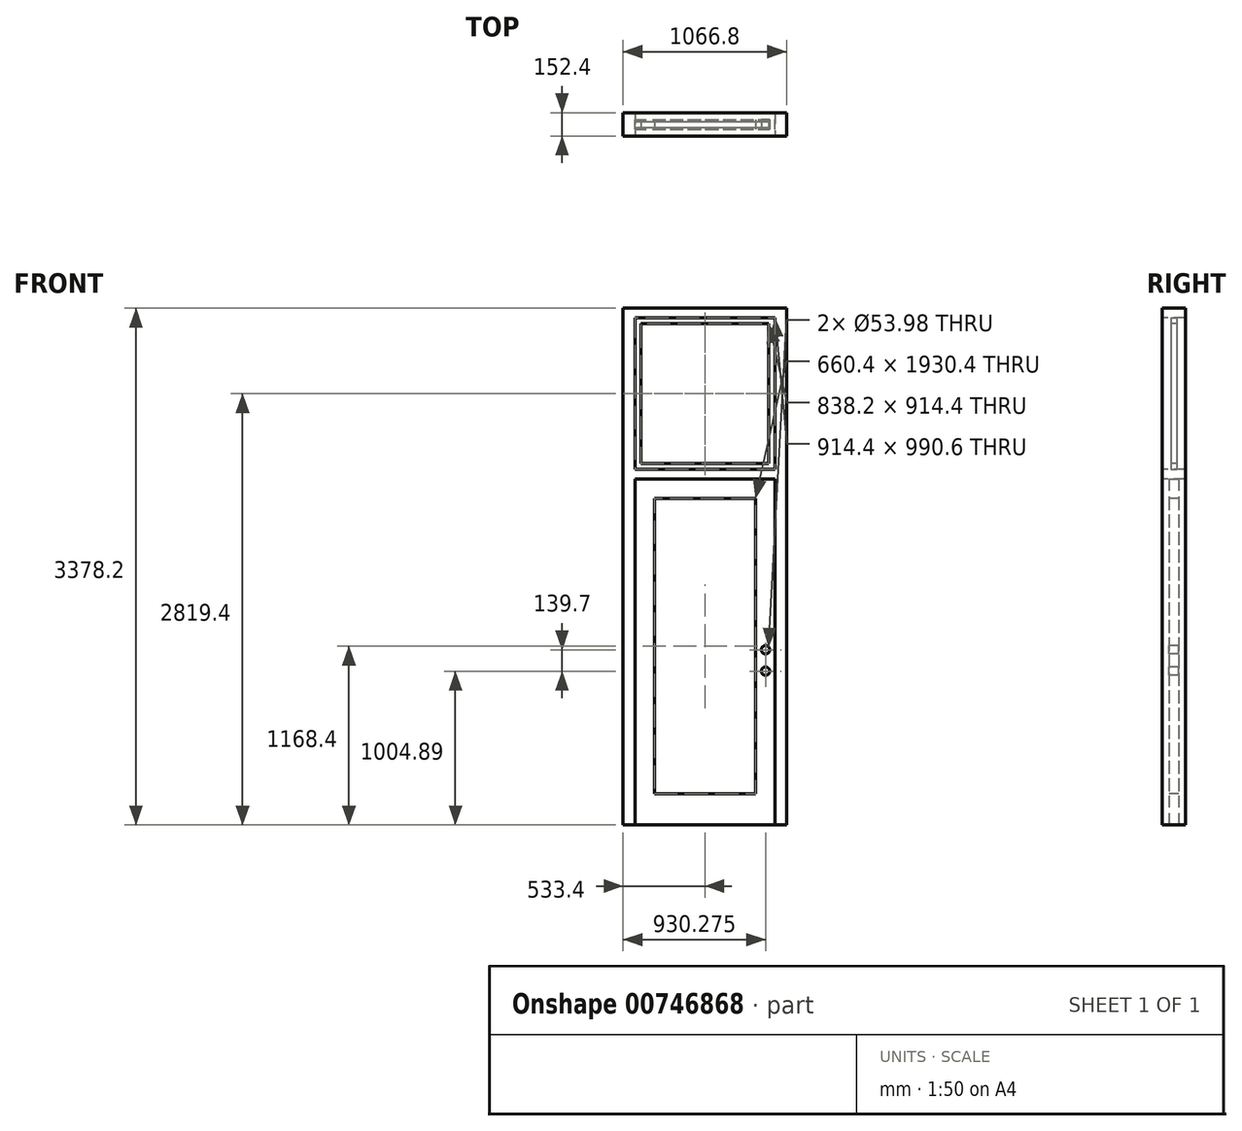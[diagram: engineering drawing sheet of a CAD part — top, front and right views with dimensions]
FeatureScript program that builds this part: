
annotation { "Feature Type Name" : "Feature", "Feature Type Description" : "" }
export const myFeature = defineFeature(function(context is Context, id is Id, definition is map)
    precondition{}
    {
        {
            var Q0;
            Q0=qCreatedBy(makeId("Front.planeOp"),FACE);
            var sketch = newSketch(context, id + "F0", { "sketchPlane" : qUnion([Q0])});
            skLineSegment(sketch, "E0.bottom", {"start": v(-533.4, 1689.1) * mm, "end": v(533.4, 1689.1) * mm});
            skLineSegment(sketch, "E0.top", {"start": v(-533.4, -1689.1) * mm, "end": v(533.4, -1689.1) * mm});
            skLineSegment(sketch, "E0.left", {"start": v(-533.4, 1689.1) * mm, "end": v(-533.4, -1689.1) * mm});
            skLineSegment(sketch, "E0.right", {"start": v(533.4, 1689.1) * mm, "end": v(533.4, -1689.1) * mm});
            skLineSegment(sketch, "E1", {"start": v(0, 1689.1) * mm, "end": v(0, 0) * mm, "construction": true});
            skLineSegment(sketch, "E2", {"start": v(0, 0) * mm, "end": v(-533.4, 0) * mm, "construction": true});
            skSolve(sketch);
        }
        {
            var Q0;
            Q0=makeQuery(id+"F0.imprint","IMPRINT",FACE,{"disambiguationData":[TD([[makeQuery(id+"F0.imprint","IMPRINT",EDGE,{"derivedFrom":sQuery(id+"F0.wireOp",EDGE,"E0.bottom")}),-1.0]])]});
            extrude(context, id + "F1", {"entities" : qUnion([Q0]), "endBound" : BoundingType.SYMMETRIC, "depth" : 152.4 * mm, "offsetDistance" : 25.4 * mm});
        }
        {
            var Q0;
            Q0=makeQuery(id+"F1.opExtrude","CAP_FACE",FACE,{"disambiguationData":[OSD([sQuery(id+"F0.wireOp",EDGE,"E0.bottom"),sQuery(id+"F0.wireOp",EDGE,"E0.top"),sQuery(id+"F0.wireOp",EDGE,"E0.left"),sQuery(id+"F0.wireOp",EDGE,"E0.right")])],"isStart":false});
            var sketch = newSketch(context, id + "F2", { "sketchPlane" : qUnion([Q0])});
            skLineSegment(sketch, "E3.bottom", {"start": v(-457.2, 571.5) * mm, "end": v(457.2, 571.5) * mm});
            skLineSegment(sketch, "E3.top", {"start": v(-457.2, -1689.1) * mm, "end": v(457.2, -1689.1) * mm});
            skLineSegment(sketch, "E3.left", {"start": v(-457.2, 571.5) * mm, "end": v(-457.2, -1689.1) * mm});
            skLineSegment(sketch, "E3.right", {"start": v(457.2, 571.5) * mm, "end": v(457.2, -1689.1) * mm});
            skLineSegment(sketch, "E4.bottom", {"start": v(-457.2, 1625.6) * mm, "end": v(457.2, 1625.6) * mm});
            skLineSegment(sketch, "E4.top", {"start": v(-457.2, 635) * mm, "end": v(457.2, 635) * mm});
            skLineSegment(sketch, "E4.left", {"start": v(-457.2, 1625.6) * mm, "end": v(-457.2, 635) * mm});
            skLineSegment(sketch, "E4.right", {"start": v(457.2, 1625.6) * mm, "end": v(457.2, 635) * mm});
            skLineSegment(sketch, "E5", {"start": v(0, 571.5) * mm, "end": v(0, 0) * mm, "construction": true});
            skSolve(sketch);
        }
        {
            var Q0;
            Q0 = qSketchRegion(id + "F2", true);
            extrude(context, id + "F3", {"entities" : qUnion([Q0]), "operationType" : NewBodyOperationType.REMOVE, "endBound" : BoundingType.THROUGH_ALL, "oppositeDirection" : true, "depth" : 25.4 * mm, "offsetDistance" : 25.4 * mm});
        }
        {
            var Q0;
            Q0=qCreatedBy(makeId("Front.planeOp"),FACE);
            var sketch = newSketch(context, id + "F4", { "sketchPlane" : qUnion([Q0])});
            skLineSegment(sketch, "E6.bottom", {"start": v(-457.2, 1625.6) * mm, "end": v(457.2, 1625.6) * mm});
            skLineSegment(sketch, "E6.top", {"start": v(-457.2, 635) * mm, "end": v(457.2, 635) * mm});
            skLineSegment(sketch, "E6.left", {"start": v(-457.2, 1625.6) * mm, "end": v(-457.2, 635) * mm});
            skLineSegment(sketch, "E6.right", {"start": v(457.2, 1625.6) * mm, "end": v(457.2, 635) * mm});
            skSolve(sketch);
        }
        {
            var Q0;
            Q0 = qSketchRegion(id + "F4", true);
            extrude(context, id + "F5", {"entities" : qUnion([Q0]), "endBound" : BoundingType.SYMMETRIC, "depth" : 38.1 * mm, "offsetDistance" : 25.4 * mm});
        }
        {
            var Q0;
            Q0=qCreatedBy(makeId("Front.planeOp"),FACE);
            var sketch = newSketch(context, id + "F6", { "sketchPlane" : qUnion([Q0])});
            skLineSegment(sketch, "E7.bottom", {"start": v(-457.2, 571.5) * mm, "end": v(457.2, 571.5) * mm});
            skLineSegment(sketch, "E7.top", {"start": v(-457.2, -1689.1) * mm, "end": v(457.2, -1689.1) * mm});
            skLineSegment(sketch, "E7.left", {"start": v(-457.2, 571.5) * mm, "end": v(-457.2, -1689.1) * mm});
            skLineSegment(sketch, "E7.right", {"start": v(457.2, 571.5) * mm, "end": v(457.2, -1689.1) * mm});
            skSolve(sketch);
        }
        {
            var Q0;
            Q0=makeQuery(id+"F6.imprint","IMPRINT",FACE,{"disambiguationData":[TD([[makeQuery(id+"F6.imprint","IMPRINT",EDGE,{"derivedFrom":sQuery(id+"F6.wireOp",EDGE,"E7.bottom")}),-1.0]])]});
            extrude(context, id + "F7", {"entities" : qUnion([Q0]), "endBound" : BoundingType.SYMMETRIC, "depth" : 63.5 * mm, "offsetDistance" : 25.4 * mm});
        }
        {
            var Q0;
            Q0=makeQuery(id+"F7.opExtrude","CAP_FACE",FACE,{"disambiguationData":[OSD([sQuery(id+"F6.wireOp",EDGE,"E7.bottom"),sQuery(id+"F6.wireOp",EDGE,"E7.top"),sQuery(id+"F6.wireOp",EDGE,"E7.left"),sQuery(id+"F6.wireOp",EDGE,"E7.right")])],"isStart":false});
            var sketch = newSketch(context, id + "F8", { "sketchPlane" : qUnion([Q0])});
            skLineSegment(sketch, "E8.bottom", {"start": v(-330.2, 444.5) * mm, "end": v(330.2, 444.5) * mm});
            skLineSegment(sketch, "E8.top", {"start": v(-330.2, -1485.9) * mm, "end": v(330.2, -1485.9) * mm});
            skLineSegment(sketch, "E8.left", {"start": v(-330.2, 444.5) * mm, "end": v(-330.2, -1485.9) * mm});
            skLineSegment(sketch, "E8.right", {"start": v(330.2, 444.5) * mm, "end": v(330.2, -1485.9) * mm});
            skSolve(sketch);
        }
        {
            var Q0;
            Q0 = qSketchRegion(id + "F8", true);
            extrude(context, id + "F9", {"entities" : qUnion([Q0]), "operationType" : NewBodyOperationType.REMOVE, "endBound" : BoundingType.THROUGH_ALL, "oppositeDirection" : true, "depth" : 25.4 * mm, "offsetDistance" : 25.4 * mm});
        }
        {
            var Q0;
            Q0=makeQuery(id+"F5.opExtrude","CAP_FACE",FACE,{"disambiguationData":[OSD([sQuery(id+"F4.wireOp",EDGE,"E6.bottom"),sQuery(id+"F4.wireOp",EDGE,"E6.top"),sQuery(id+"F4.wireOp",EDGE,"E6.left"),sQuery(id+"F4.wireOp",EDGE,"E6.right")])],"isStart":false});
            var sketch = newSketch(context, id + "F10", { "sketchPlane" : qUnion([Q0])});
            skLineSegment(sketch, "E9.bottom", {"start": v(-419.1, 1587.5) * mm, "end": v(419.1, 1587.5) * mm});
            skLineSegment(sketch, "E9.top", {"start": v(-419.1, 673.1) * mm, "end": v(419.1, 673.1) * mm});
            skLineSegment(sketch, "E9.left", {"start": v(-419.1, 1587.5) * mm, "end": v(-419.1, 673.1) * mm});
            skLineSegment(sketch, "E9.right", {"start": v(419.1, 1587.5) * mm, "end": v(419.1, 673.1) * mm});
            skSolve(sketch);
        }
        {
            var Q0;
            Q0 = qSketchRegion(id + "F10", true);
            extrude(context, id + "F11", {"entities" : qUnion([Q0]), "operationType" : NewBodyOperationType.REMOVE, "endBound" : BoundingType.THROUGH_ALL, "oppositeDirection" : true, "depth" : 25.4 * mm, "offsetDistance" : 25.4 * mm});
        }
        {
            var Q0;
            Q0=makeQuery(id+"F7.opExtrude","CAP_FACE",FACE,{"disambiguationData":[OSD([sQuery(id+"F6.wireOp",EDGE,"E7.bottom"),sQuery(id+"F6.wireOp",EDGE,"E7.top"),sQuery(id+"F6.wireOp",EDGE,"E7.left"),sQuery(id+"F6.wireOp",EDGE,"E7.right")])],"isStart":false});
            var sketch = newSketch(context, id + "F12", { "sketchPlane" : qUnion([Q0])});
            skCircle(sketch, "E10", {"center": v(396.88, -544.51) * mm, "radius": 26.99 * mm});
            skPoint(sketch, "E10.perimeterSnap0", {"position": v(330.2, -520.7) * mm});
            skCircle(sketch, "E11", {"center": v(396.88, -684.21) * mm, "radius": 26.99 * mm});
            skSolve(sketch);
        }
        {
            var Q0;
            Q0=makeQuery(id+"F12.imprint","IMPRINT",FACE,{"disambiguationData":[TD([[makeQuery(id+"F12.imprint","IMPRINT",EDGE,{"derivedFrom":sQuery(id+"F12.wireOp",EDGE,"E11")}),1.0]])]});
            var Q1;
            Q1=makeQuery(id+"F12.imprint","IMPRINT",FACE,{"disambiguationData":[TD([[makeQuery(id+"F12.imprint","IMPRINT",EDGE,{"derivedFrom":sQuery(id+"F12.wireOp",EDGE,"E10")}),1.0]])]});
            extrude(context, id + "F13", {"entities" : qUnion([Q0, Q1]), "operationType" : NewBodyOperationType.REMOVE, "endBound" : BoundingType.THROUGH_ALL, "oppositeDirection" : true, "depth" : 25.4 * mm, "offsetDistance" : 25.4 * mm});
        }
    });
